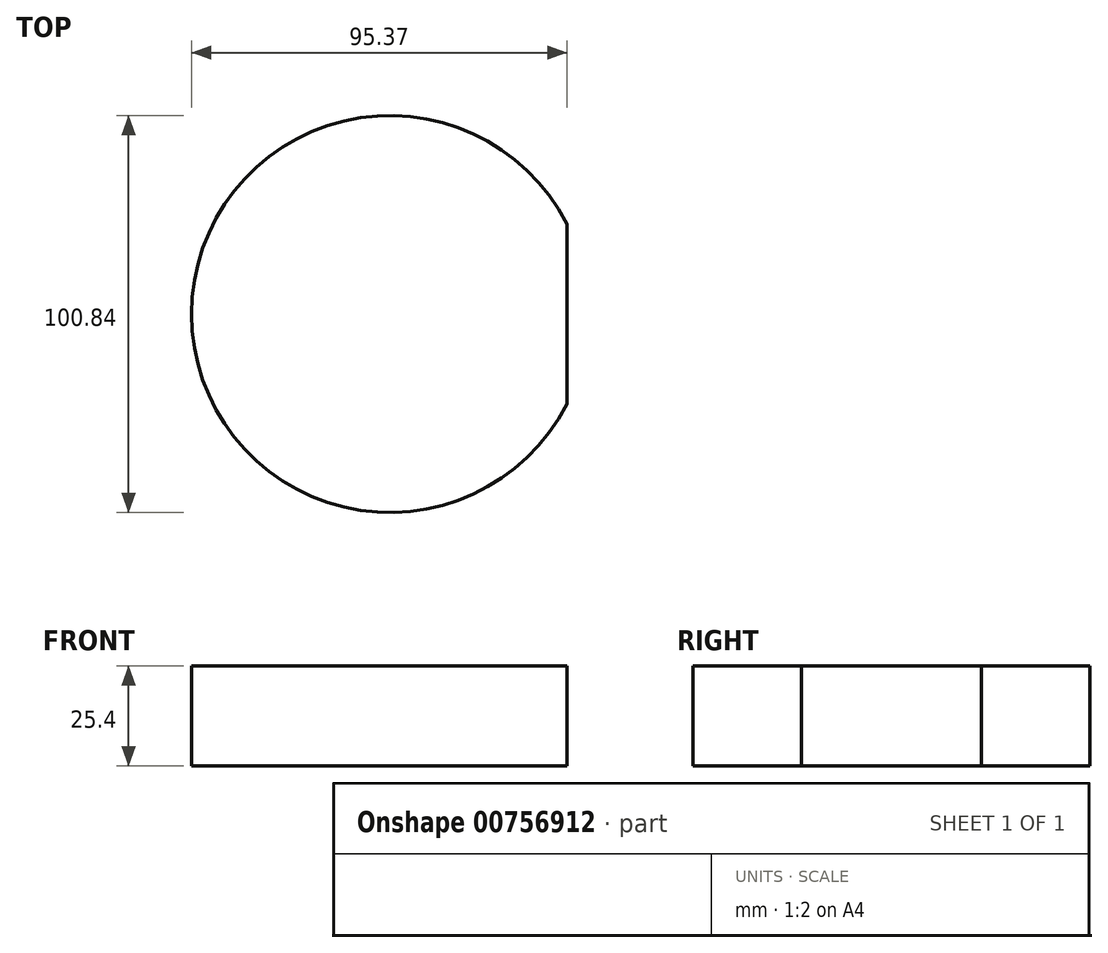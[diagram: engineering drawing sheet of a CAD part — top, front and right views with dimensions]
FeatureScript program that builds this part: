
annotation { "Feature Type Name" : "Feature", "Feature Type Description" : "" }
export const myFeature = defineFeature(function(context is Context, id is Id, definition is map)
    precondition{}
    {
        {
            var Q0;
            Q0=qCreatedBy(makeId("Top.planeOp"),FACE);
            var sketch = newSketch(context, id + "F0", { "sketchPlane" : qUnion([Q0])});
            skArc(sketch, "E0", {"start": v(44.95, 22.84) * mm, "mid": v(-50.42, 0) * mm, "end": v(44.95, -22.84) * mm});
            skLineSegment(sketch, "E1.bottom", {"start": v(44.95, -22.84) * mm, "end": v(76.94, -22.84) * mm});
            skLineSegment(sketch, "E1.top", {"start": v(44.95, 23.23) * mm, "end": v(76.94, 23.23) * mm});
            skLineSegment(sketch, "E1.left", {"start": v(44.95, 22.84) * mm, "end": v(44.95, 23.23) * mm});
            skLineSegment(sketch, "E1.right", {"start": v(76.94, -22.84) * mm, "end": v(76.94, 23.23) * mm});
            skLineSegment(sketch, "E2", {"start": v(44.95, -22.84) * mm, "end": v(44.95, 22.84) * mm});
            skSolve(sketch);
        }
        {
            var Q0;
            Q0=makeQuery(id+"F0.imprint","IMPRINT",FACE,{"disambiguationData":[TD([[makeQuery(id+"F0.imprint","IMPRINT",EDGE,{"derivedFrom":sQuery(id+"F0.wireOp",EDGE,"E0")}),1.0]])]});
            extrude(context, id + "F1", {"entities" : qUnion([Q0]), "depth" : 25.4 * mm, "offsetDistance" : 25.4 * mm});
        }
    });
